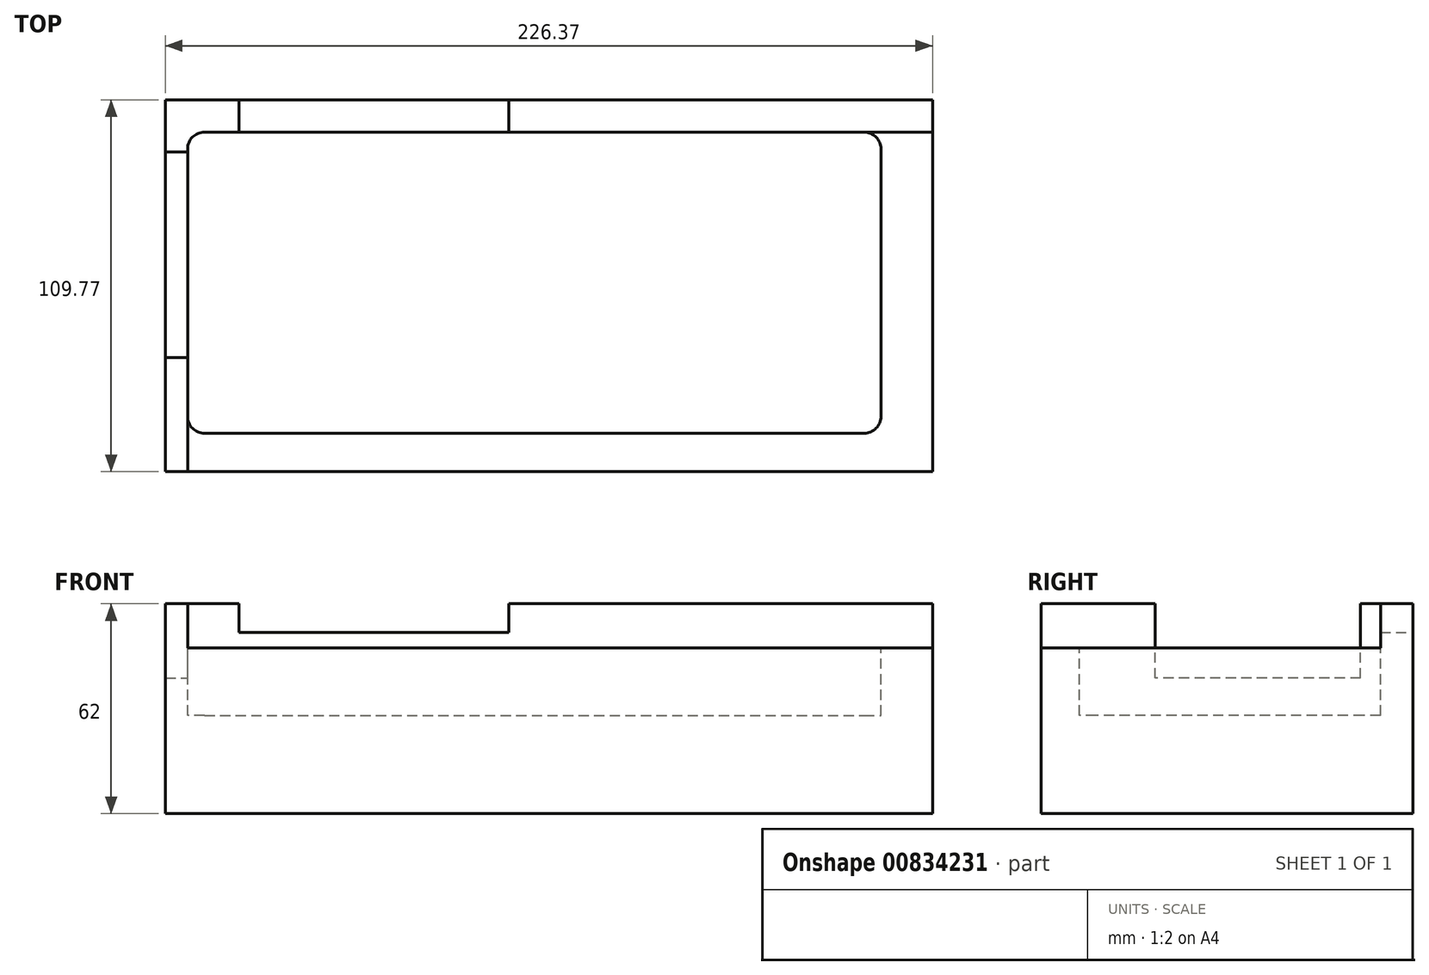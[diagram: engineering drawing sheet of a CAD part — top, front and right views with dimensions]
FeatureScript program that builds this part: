
annotation { "Feature Type Name" : "Feature", "Feature Type Description" : "" }
export const myFeature = defineFeature(function(context is Context, id is Id, definition is map)
    precondition{}
    {
        {
            var Q0;
            Q0=qCreatedBy(makeId("Top.planeOp"),FACE);
            var sketch = newSketch(context, id + "F0", { "sketchPlane" : qUnion([Q0])});
            skLineSegment(sketch, "E0.bottom", {"start": v(-115.7, 54.44) * mm, "end": v(110.67, 54.44) * mm});
            skLineSegment(sketch, "E0.top", {"start": v(-115.7, -55.33) * mm, "end": v(110.67, -55.33) * mm});
            skLineSegment(sketch, "E0.left", {"start": v(-115.7, 54.44) * mm, "end": v(-115.7, -55.33) * mm});
            skLineSegment(sketch, "E0.right", {"start": v(110.67, 54.44) * mm, "end": v(110.67, -55.33) * mm});
            skSolve(sketch);
        }
        {
            var Q0;
            Q0=makeQuery(id+"F0.imprint","IMPRINT",FACE,{"disambiguationData":[TD([[makeQuery(id+"F0.imprint","IMPRINT",EDGE,{"derivedFrom":sQuery(id+"F0.wireOp",EDGE,"E0.bottom")}),-1.0]])]});
            extrude(context, id + "F1", {"entities" : qUnion([Q0]), "depth" : 62 * mm, "offsetDistance" : 25 * mm});
        }
        {
            var Q0;
            Q0=makeQuery(id+"F1.opExtrude","CAP_FACE",FACE,{"disambiguationData":[OSD([sQuery(id+"F0.wireOp",EDGE,"E0.bottom"),sQuery(id+"F0.wireOp",EDGE,"E0.top"),sQuery(id+"F0.wireOp",EDGE,"E0.left"),sQuery(id+"F0.wireOp",EDGE,"E0.right")])],"isStart":false});
            var sketch = newSketch(context, id + "F2", { "sketchPlane" : qUnion([Q0])});
            skLineSegment(sketch, "E1.bottom", {"start": v(-109.17, 44.88) * mm, "end": v(137.46, 44.88) * mm});
            skLineSegment(sketch, "E1.top", {"start": v(-109.17, -77.33) * mm, "end": v(137.46, -77.33) * mm});
            skLineSegment(sketch, "E1.left", {"start": v(-109.17, 44.88) * mm, "end": v(-109.17, -77.33) * mm});
            skLineSegment(sketch, "E1.right", {"start": v(137.46, 44.88) * mm, "end": v(137.46, -77.33) * mm});
            skSolve(sketch);
        }
        {
            var Q0;
            {var subQ0=sQuery(id+"F2.wireOp",EDGE,"E1.left");var subQ1=sQuery(id+"F2.wireOp",EDGE,"E1.bottom");var subQ2=makeQuery(id+"F2.imprint","INTERSECT",VERTEX,{"derivedFrom":[subQ1,subQ0]});Q0=makeQuery(id+"F2.imprint","IMPRINT",FACE,{"disambiguationData":[TD([[makeQuery(id+"F2.imprint","IMPRINT",EDGE,{"disambiguationData":[TD([[subQ2,-1.0]])],"derivedFrom":subQ1}),-1.0]])]});}
            extrude(context, id + "F3", {"entities" : qUnion([Q0]), "operationType" : NewBodyOperationType.REMOVE, "oppositeDirection" : true, "depth" : 13 * mm, "offsetDistance" : 25 * mm});
        }
        {
            var Q0;
            Q0=makeQuery(id+"F1.opExtrude","CAP_FACE",FACE,{"disambiguationData":[OSD([sQuery(id+"F0.wireOp",EDGE,"E0.bottom"),sQuery(id+"F0.wireOp",EDGE,"E0.top"),sQuery(id+"F0.wireOp",EDGE,"E0.left"),sQuery(id+"F0.wireOp",EDGE,"E0.right")])],"isStart":false});
            var sketch = newSketch(context, id + "F4", { "sketchPlane" : qUnion([Q0])});
            skLineSegment(sketch, "E2.bottom", {"start": v(-115.7, 39.01) * mm, "end": v(-109.17, 39.01) * mm});
            skLineSegment(sketch, "E2.top", {"start": v(-115.7, -21.66) * mm, "end": v(-109.17, -21.66) * mm});
            skLineSegment(sketch, "E2.left", {"start": v(-115.7, 39.01) * mm, "end": v(-115.7, -21.66) * mm});
            skLineSegment(sketch, "E2.right", {"start": v(-109.17, 39.01) * mm, "end": v(-109.17, -21.66) * mm});
            skSolve(sketch);
        }
        {
            var Q0;
            Q0=makeQuery(id+"F4.imprint","IMPRINT",FACE,{"disambiguationData":[TD([[makeQuery(id+"F4.imprint","IMPRINT",EDGE,{"derivedFrom":sQuery(id+"F4.wireOp",EDGE,"E2.bottom")}),-1.0]])]});
            extrude(context, id + "F5", {"entities" : qUnion([Q0]), "operationType" : NewBodyOperationType.REMOVE, "oppositeDirection" : true, "depth" : 22 * mm, "offsetDistance" : 25 * mm});
        }
        {
            var Q0;
            Q0=makeQuery(id+"F3.boolean.opBoolean","COPY",FACE,{"derivedFrom":makeQuery(id+"F3.opExtrude","CAP_FACE",FACE,{"disambiguationData":[OSD([sQuery(id+"F0.wireOp",EDGE,"E0.top"),sQuery(id+"F0.wireOp",EDGE,"E0.right"),sQuery(id+"F2.wireOp",EDGE,"E1.bottom"),sQuery(id+"F2.wireOp",EDGE,"E1.left")])],"isStart":false})});
            var sketch = newSketch(context, id + "F6", { "sketchPlane" : qUnion([Q0])});
            skLineSegment(sketch, "E3.bottom", {"start": v(-109.17, 44.88) * mm, "end": v(95.5, 44.88) * mm});
            skLineSegment(sketch, "E3.top", {"start": v(-109.17, -44) * mm, "end": v(95.5, -44) * mm});
            skLineSegment(sketch, "E3.left", {"start": v(-109.17, 44.88) * mm, "end": v(-109.17, -44) * mm});
            skLineSegment(sketch, "E3.right", {"start": v(95.5, 44.88) * mm, "end": v(95.5, -44) * mm});
            skSolve(sketch);
        }
        {
            var Q0;
            {var subQ3=sQuery(id+"F6.wireOp",EDGE,"E3.bottom");Q0=makeQuery(id+"F6.imprint","IMPRINT",FACE,{"disambiguationData":[TD([[makeQuery(id+"F6.imprint","IMPRINT",EDGE,{"derivedFrom":subQ3}),-1.0]])]});}
            extrude(context, id + "F7", {"entities" : qUnion([Q0]), "operationType" : NewBodyOperationType.REMOVE, "oppositeDirection" : true, "depth" : 20 * mm, "offsetDistance" : 25 * mm});
        }
        {
            var Q0;
            Q0=makeQuery(id+"F7.boolean.opBoolean","COPY",EDGE,{"derivedFrom":makeQuery(id+"F7.opExtrude","SWEPT_EDGE",EDGE,{"disambiguationData":[OSD([sQuery(id+"F2.wireOp",EDGE,"E1.bottom"),sQuery(id+"F6.wireOp",EDGE,"E3.bottom"),sQuery(id+"F6.wireOp",EDGE,"E3.right")])]})});
            fillet(context, id + "F8", {"entities" : qUnion([Q0]), "radius" : 5 * mm, "tangentPropagation" : true, "allowEdgeOverflow" : false});
        }
        {
            var Q0;
            Q0=makeQuery(id+"F7.boolean.opBoolean","COPY",EDGE,{"derivedFrom":makeQuery(id+"F7.opExtrude","SWEPT_EDGE",EDGE,{"disambiguationData":[OSD([sQuery(id+"F6.wireOp",EDGE,"E3.top"),sQuery(id+"F6.wireOp",EDGE,"E3.right")])]})});
            fillet(context, id + "F9", {"entities" : qUnion([Q0]), "radius" : 5 * mm, "tangentPropagation" : true, "allowEdgeOverflow" : false});
        }
        {
            var Q0;
            Q0=makeQuery(id+"F7.boolean.opBoolean","COPY",EDGE,{"derivedFrom":makeQuery(id+"F7.opExtrude","SWEPT_EDGE",EDGE,{"disambiguationData":[OSD([sQuery(id+"F2.wireOp",EDGE,"E1.left"),sQuery(id+"F6.wireOp",EDGE,"E3.top"),sQuery(id+"F6.wireOp",EDGE,"E3.left")])]})});
            fillet(context, id + "F10", {"entities" : qUnion([Q0]), "radius" : 5 * mm, "tangentPropagation" : true, "allowEdgeOverflow" : false});
        }
        {
            var Q0;
            Q0=makeQuery(id+"F7.boolean.opBoolean","MERGE",EDGE,{"derivedFrom":[makeQuery(id+"F3.boolean.opBoolean","COPY",EDGE,{"derivedFrom":makeQuery(id+"F3.opExtrude","SWEPT_EDGE",EDGE,{"disambiguationData":[OSD([sQuery(id+"F2.wireOp",EDGE,"E1.bottom"),sQuery(id+"F2.wireOp",EDGE,"E1.left")])]})}),makeQuery(id+"F7.opExtrude","SWEPT_EDGE",EDGE,{"disambiguationData":[OSD([sQuery(id+"F6.wireOp",EDGE,"E3.bottom"),sQuery(id+"F6.wireOp",EDGE,"E3.left")])]})]});
            fillet(context, id + "F11", {"entities" : qUnion([Q0]), "radius" : 5 * mm, "tangentPropagation" : true, "allowEdgeOverflow" : false});
        }
        {
            var Q0;
            Q0=makeQuery(id+"F1.opExtrude","SWEPT_FACE",FACE,{"disambiguationData":[OSD([sQuery(id+"F0.wireOp",EDGE,"E0.bottom")])]});
            var sketch = newSketch(context, id + "F12", { "sketchPlane" : qUnion([Q0])});
            skLineSegment(sketch, "E4.bottom", {"start": v(94.01, 62) * mm, "end": v(14.4, 62) * mm});
            skLineSegment(sketch, "E4.top", {"start": v(94.01, 53.53) * mm, "end": v(14.4, 53.53) * mm});
            skLineSegment(sketch, "E4.left", {"start": v(94.01, 62) * mm, "end": v(94.01, 53.53) * mm});
            skLineSegment(sketch, "E4.right", {"start": v(14.4, 62) * mm, "end": v(14.4, 53.53) * mm});
            skSolve(sketch);
        }
        {
            var Q0;
            Q0=makeQuery(id+"F12.imprint","IMPRINT",FACE,{"disambiguationData":[TD([[makeQuery(id+"F12.imprint","IMPRINT",EDGE,{"derivedFrom":sQuery(id+"F12.wireOp",EDGE,"E4.bottom")}),1.0]])]});
            extrude(context, id + "F13", {"entities" : qUnion([Q0]), "operationType" : NewBodyOperationType.REMOVE, "oppositeDirection" : true, "depth" : 25 * mm, "offsetDistance" : 25 * mm});
        }
    });
